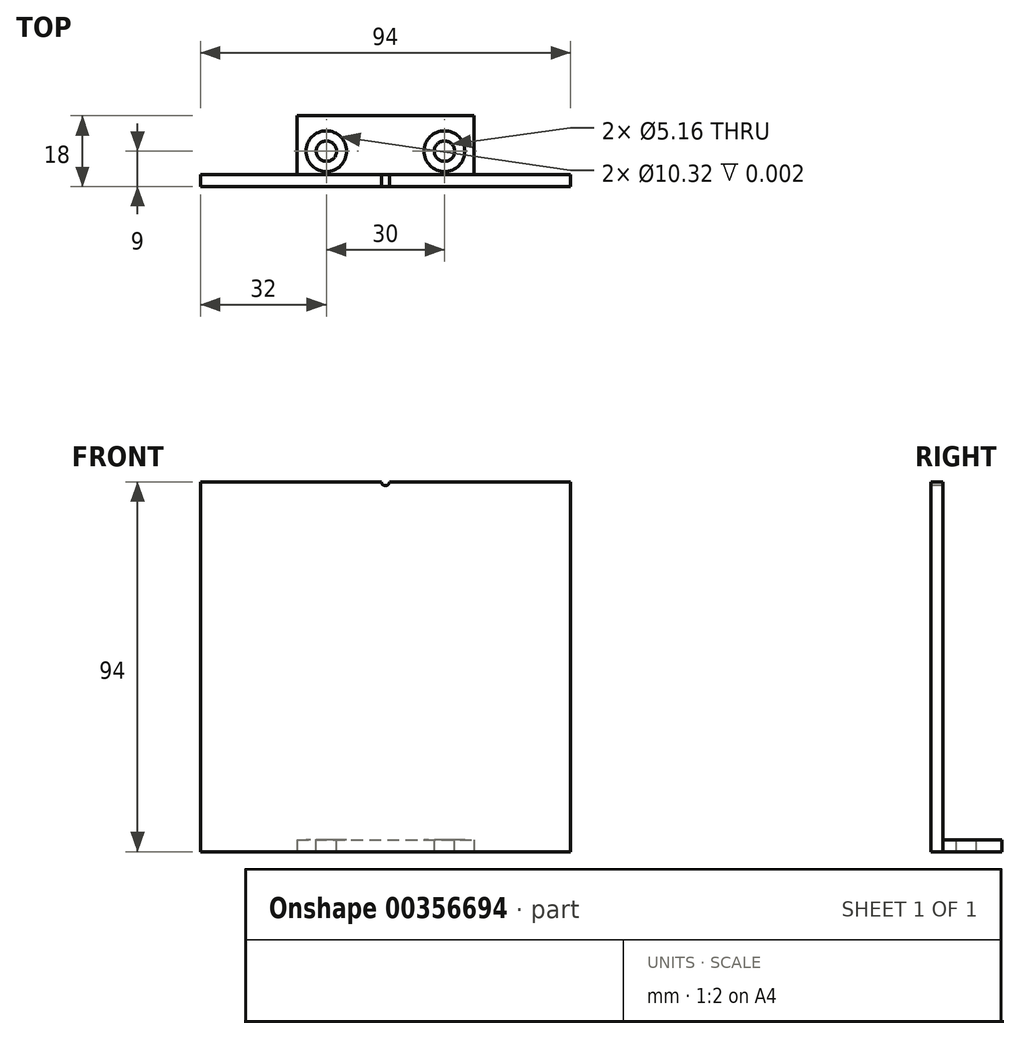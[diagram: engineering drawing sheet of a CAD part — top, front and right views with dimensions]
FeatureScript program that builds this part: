
annotation { "Feature Type Name" : "Feature", "Feature Type Description" : "" }
export const myFeature = defineFeature(function(context is Context, id is Id, definition is map)
    precondition{}
    {
        {
            var Q0;
            Q0=qCreatedBy(makeId("Front.planeOp"),FACE);
            var sketch = newSketch(context, id + "F0", { "sketchPlane" : qUnion([Q0])});
            skLineSegment(sketch, "E0.bottom", {"start": v(-47, 47) * mm, "end": v(47, 47) * mm});
            skLineSegment(sketch, "E0.top", {"start": v(-47, -47) * mm, "end": v(47, -47) * mm});
            skLineSegment(sketch, "E0.left", {"start": v(-47, 47) * mm, "end": v(-47, -47) * mm});
            skLineSegment(sketch, "E0.right", {"start": v(47, 47) * mm, "end": v(47, -47) * mm});
            skLineSegment(sketch, "E1.bottom", {"start": v(-50, 50) * mm, "end": v(50, 50) * mm, "construction": true});
            skLineSegment(sketch, "E1.top", {"start": v(-50, -50) * mm, "end": v(50, -50) * mm, "construction": true});
            skLineSegment(sketch, "E1.left", {"start": v(-50, 50) * mm, "end": v(-50, -50) * mm, "construction": true});
            skLineSegment(sketch, "E1.right", {"start": v(50, 50) * mm, "end": v(50, -50) * mm, "construction": true});
            skSolve(sketch);
        }
        {
            var Q0;
            Q0=qSketchRegion(id+"F0",true);
            extrude(context, id + "F1", {"entities" : qUnion([Q0]), "depth" : 3 * mm});
        }
        {
            var Q0;
            Q0=makeQuery(id+"F1.opExtrude","SWEPT_FACE",FACE,{"disambiguationData":[OSD([sQuery(id+"F0.wireOp",EDGE,"E0.top")])]});
            var sketch = newSketch(context, id + "F2", { "sketchPlane" : qUnion([Q0])});
            skLineSegment(sketch, "E2.0", {"start": v(-22.5, 0) * mm, "end": v(22.5, 0) * mm});
            skLineSegment(sketch, "E3", {"start": v(-22.5, 0) * mm, "end": v(-22.5, -15) * mm});
            skLineSegment(sketch, "E4", {"start": v(-22.5, -15) * mm, "end": v(22.5, -15) * mm});
            skLineSegment(sketch, "E5", {"start": v(22.5, -15) * mm, "end": v(22.5, 0) * mm});
            skPoint(sketch, "E6.orphan", {"position": v(-47, 0) * mm});
            skPoint(sketch, "E7.orphan", {"position": v(47, 0) * mm});
            skSolve(sketch);
        }
        {
            var Q0;
            Q0=makeQuery(id+"F2.imprint","IMPRINT",FACE,{"disambiguationData":[TD([[makeQuery(id+"F2.imprint","IMPRINT",EDGE,{"derivedFrom":sQuery(id+"F2.wireOp",EDGE,"E2.0")}),-1.0]])]});
            extrude(context, id + "F3", {"entities" : qUnion([Q0]), "operationType" : NewBodyOperationType.ADD, "oppositeDirection" : true, "depth" : 3 * mm});
        }
        {
            var Q0;
            Q0=makeQuery(id+"F3.opExtrude","CAP_FACE",FACE,{"disambiguationData":[OSD([sQuery(id+"F2.wireOp",EDGE,"E2.0"),sQuery(id+"F2.wireOp",EDGE,"E3"),sQuery(id+"F2.wireOp",EDGE,"E4"),sQuery(id+"F2.wireOp",EDGE,"E5")])],"isStart":false});
            var sketch = newSketch(context, id + "F4", { "sketchPlane" : qUnion([Q0])});
            skCircle(sketch, "E8", {"center": v(-15, 6) * mm, "radius": 2.58 * mm});
            skCircle(sketch, "E9", {"center": v(15, 6) * mm, "radius": 2.58 * mm});
            skSolve(sketch);
        }
        {
            var Q0;
            Q0=qSketchRegion(id+"F4",true);
            extrude(context, id + "F5", {"entities" : qUnion([Q0]), "operationType" : NewBodyOperationType.REMOVE, "endBound" : BoundingType.THROUGH_ALL, "oppositeDirection" : true, "depth" : 25 * mm});
        }
        {
            var Q0;
            Q0=makeQuery(id+"F3.opExtrude","CAP_FACE",FACE,{"disambiguationData":[OSD([sQuery(id+"F2.wireOp",EDGE,"E2.0"),sQuery(id+"F2.wireOp",EDGE,"E3"),sQuery(id+"F2.wireOp",EDGE,"E4"),sQuery(id+"F2.wireOp",EDGE,"E5")])],"isStart":false});
            var sketch = newSketch(context, id + "F6", { "sketchPlane" : qUnion([Q0])});
            skCircle(sketch, "E10", {"center": v(-15, 6) * mm, "radius": 5.16 * mm});
            skCircle(sketch, "E11", {"center": v(15, 6) * mm, "radius": 5.16 * mm});
            skSolve(sketch);
        }
        {
            var Q0;
            Q0=qSketchRegion(id+"F6",true);
            extrude(context, id + "F7", {"entities" : qUnion([Q0]), "operationType" : NewBodyOperationType.REMOVE, "oppositeDirection" : true, "depth" : 1 / 406.4 * mm});
        }
        {
            var Q0;
            Q0=makeQuery(id+"F1.opExtrude","CAP_FACE",FACE,{"disambiguationData":[OSD([sQuery(id+"F0.wireOp",EDGE,"E0.bottom"),sQuery(id+"F0.wireOp",EDGE,"E0.top"),sQuery(id+"F0.wireOp",EDGE,"E0.left"),sQuery(id+"F0.wireOp",EDGE,"E0.right")])],"isStart":false});
            var sketch = newSketch(context, id + "F8", { "sketchPlane" : qUnion([Q0])});
            skCircle(sketch, "E12", {"center": v(0, 47) * mm, "radius": 1 * mm});
            skSolve(sketch);
        }
        {
            var Q0;
            Q0=qSketchRegion(id+"F8",true);
            extrude(context, id + "F9", {"entities" : qUnion([Q0]), "operationType" : NewBodyOperationType.REMOVE, "endBound" : BoundingType.THROUGH_ALL, "oppositeDirection" : true, "depth" : 25 * mm});
        }
    });
